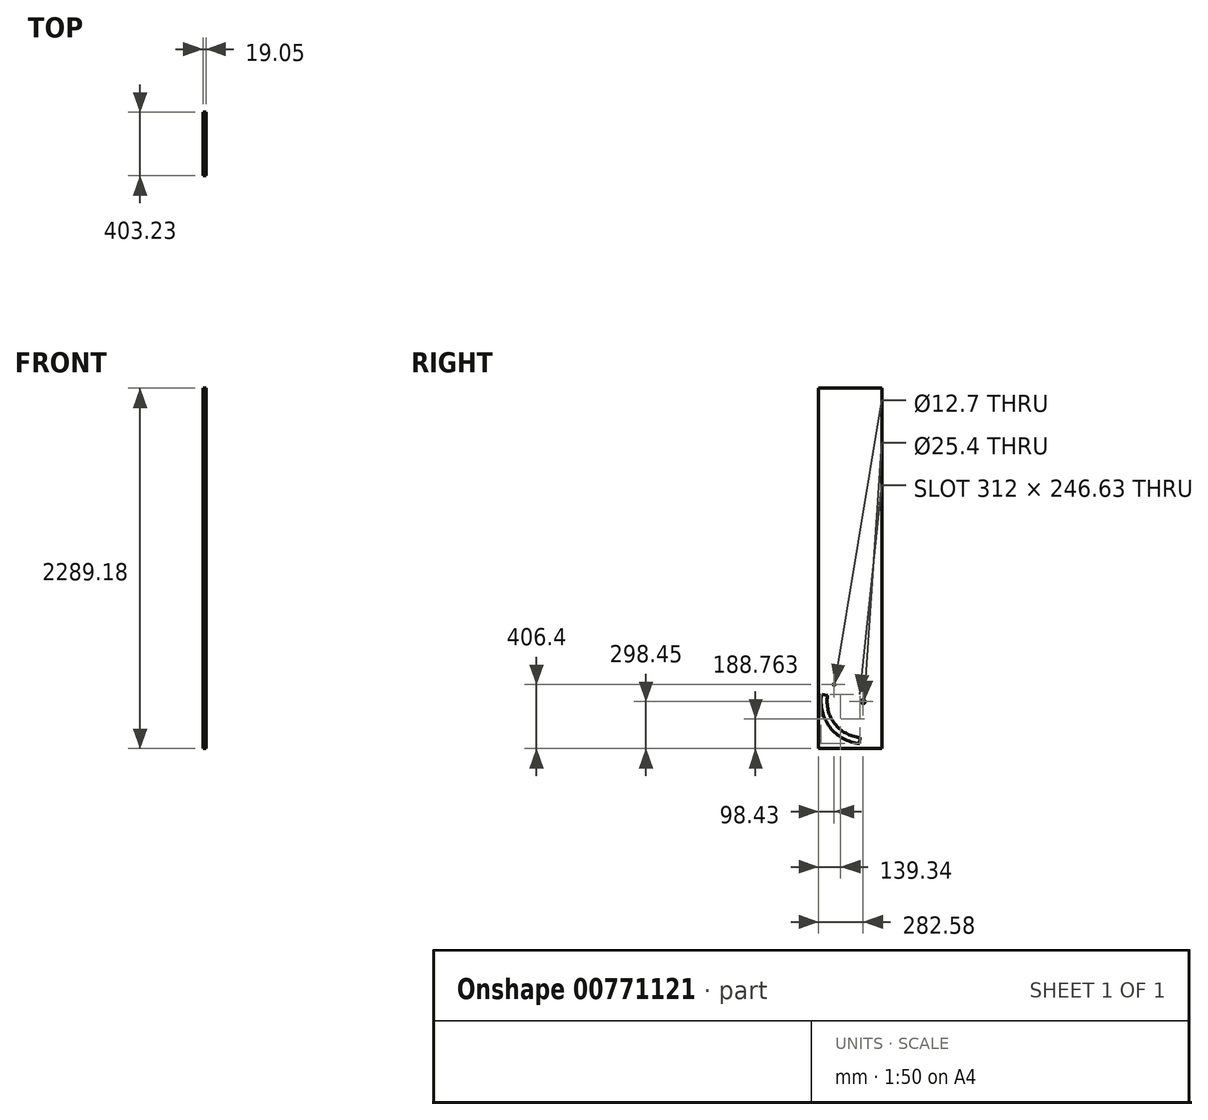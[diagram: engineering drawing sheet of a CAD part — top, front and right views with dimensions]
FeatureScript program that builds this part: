
annotation { "Feature Type Name" : "Feature", "Feature Type Description" : "" }
export const myFeature = defineFeature(function(context is Context, id is Id, definition is map)
    precondition{}
    {
        {
            var Q0;
            Q0=qCreatedBy(makeId("Right.planeOp"),FACE);
            var sketch = newSketch(context, id + "F0", { "sketchPlane" : qUnion([Q0])});
            skLineSegment(sketch, "E0.bottom", {"start": v(0, 0) * mm, "end": v(-403.23, 0) * mm});
            skLineSegment(sketch, "E0.top", {"start": v(0, 2289.18) * mm, "end": v(-403.23, 2289.18) * mm});
            skLineSegment(sketch, "E0.left", {"start": v(0, 0) * mm, "end": v(0, 2289.18) * mm});
            skLineSegment(sketch, "E0.right", {"start": v(-403.23, 0) * mm, "end": v(-403.23, 2289.18) * mm});
            skPoint(sketch, "E1", {"position": v(-120.65, 298.45) * mm});
            skPoint(sketch, "E2", {"position": v(-304.8, 406.4) * mm});
            skArc(sketch, "E3", {"start": v(-345.78, 338.15) * mm, "mid": v(-302.01, 159.29) * mm, "end": v(-140.57, 70.72) * mm});
            skArc(sketch, "E4", {"start": v(-383.3, 344.76) * mm, "mid": v(-332.24, 136.1) * mm, "end": v(-143.9, 32.76) * mm});
            skLineSegment(sketch, "E5", {"start": v(-140.57, 70.72) * mm, "end": v(-143.9, 32.76) * mm});
            skLineSegment(sketch, "E6", {"start": v(-383.3, 344.76) * mm, "end": v(-345.78, 338.15) * mm});
            skLineSegment(sketch, "E7", {"start": v(-120.65, 298.45) * mm, "end": v(-345.78, 338.15) * mm, "construction": true});
            skLineSegment(sketch, "E8", {"start": v(-120.65, 298.45) * mm, "end": v(-140.57, 70.72) * mm, "construction": true});
            skCircle(sketch, "E9", {"center": v(-304.8, 406.4) * mm, "radius": 6.35 * mm});
            skSolve(sketch);
        }
        {
            var Q0;
            Q0 = qSketchRegion(id + "F0", true);
            extrude(context, id + "F1", {"entities" : qUnion([Q0]), "depth" : 19.05 * mm, "offsetDistance" : 25.4 * mm});
        }
        {
            var Q0;
            Q0=sQuery(id+"F0.wireOp",VERTEX,"E1");
            var Q1;
            Q1=makeQuery(id+"F1.opExtrude","SWEPT_BODY",BODY,{"disambiguationData":[OSD([sQuery(id+"F0.wireOp",EDGE,"E0.bottom"),sQuery(id+"F0.wireOp",EDGE,"E0.top"),sQuery(id+"F0.wireOp",EDGE,"E0.left"),sQuery(id+"F0.wireOp",EDGE,"E0.right")])]});
            hole(context, id + "F2", {"style" : HoleStyle.SIMPLE, "endStyle" : HoleEndStyle.THROUGH, "oppositeDirection" : true, "holeDiameter" : 25.4 * mm, "majorDiameter" : 6.35 * mm, "isTappedThrough" : true, "tappedDepth" : 12.7 * mm, "tapClearance" : 3, "locations" : qUnion([Q0]), "scope" : qUnion([Q1])});
        }
    });
